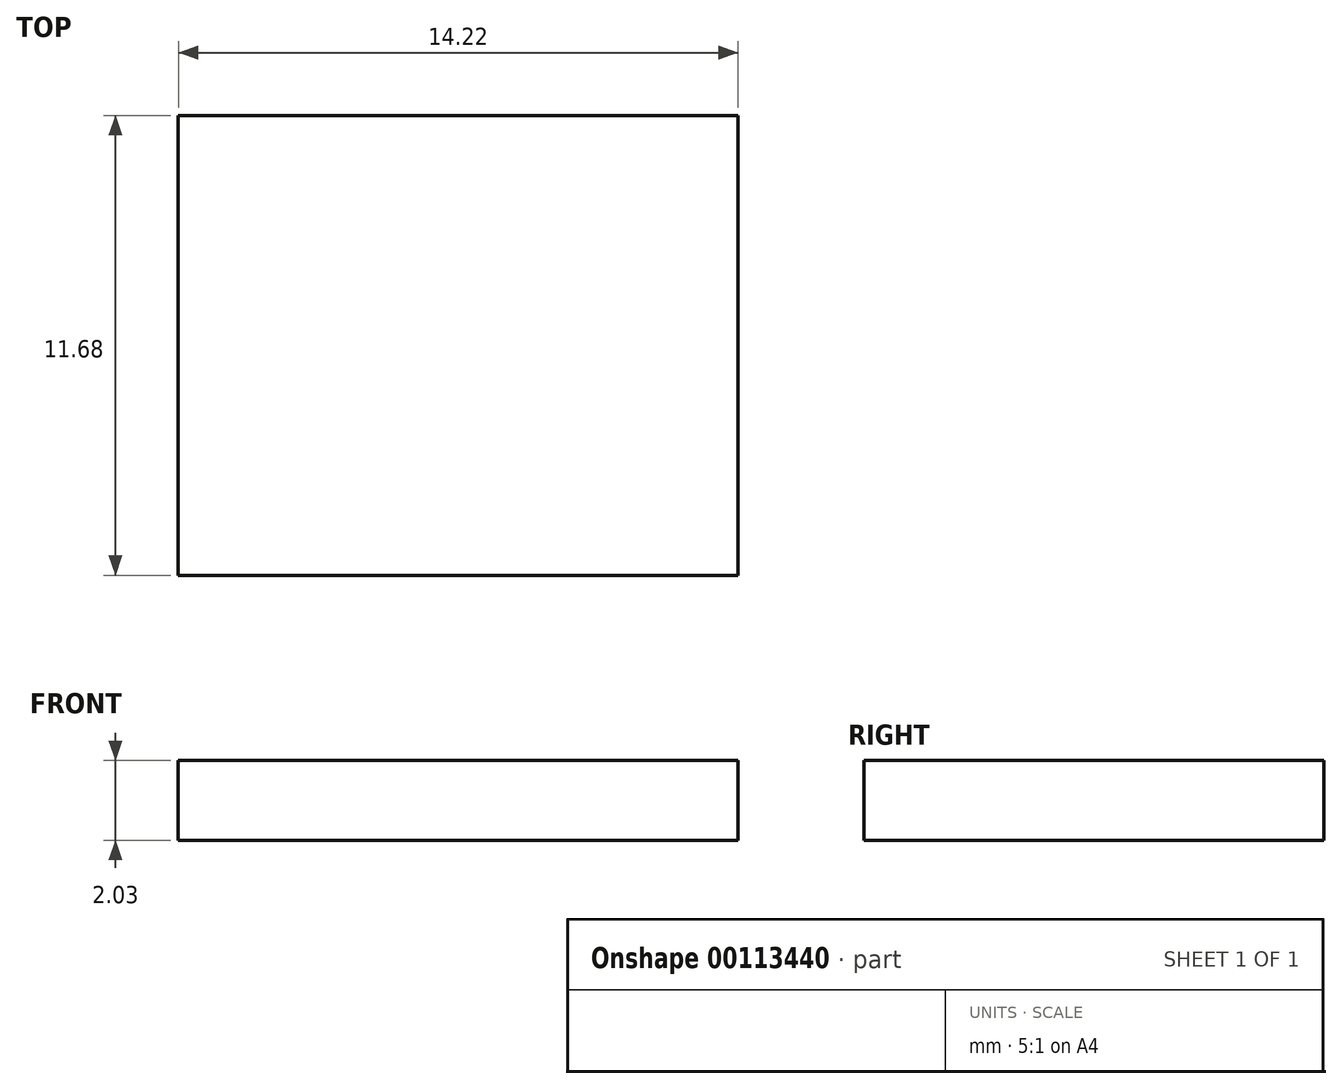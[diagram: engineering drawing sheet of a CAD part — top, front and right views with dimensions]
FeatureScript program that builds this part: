
annotation { "Feature Type Name" : "Feature", "Feature Type Description" : "" }
export const myFeature = defineFeature(function(context is Context, id is Id, definition is map)
    precondition{}
    {
        {
            var Q0;
            Q0=qCreatedBy(makeId("Top.planeOp"),FACE);
            var sketch = newSketch(context, id + "F0", { "sketchPlane" : qUnion([Q0])});
            skLineSegment(sketch, "E0.bottom", {"start": v(7.11, 5.84) * mm, "end": v(-7.11, 5.84) * mm});
            skLineSegment(sketch, "E0.top", {"start": v(7.11, -5.84) * mm, "end": v(-7.11, -5.84) * mm});
            skLineSegment(sketch, "E0.left", {"start": v(7.11, 5.84) * mm, "end": v(7.11, -5.84) * mm});
            skLineSegment(sketch, "E0.right", {"start": v(-7.11, 5.84) * mm, "end": v(-7.11, -5.84) * mm});
            skPoint(sketch, "E0.middle", {"position": v(0, 0) * mm});
            skSolve(sketch);
        }
        {
            var Q0;
            Q0=makeQuery(id+"F0.imprint","IMPRINT",FACE,{"disambiguationData":[TD([[makeQuery(id+"F0.imprint","IMPRINT",EDGE,{"derivedFrom":sQuery(id+"F0.wireOp",EDGE,"E0.bottom")}),1.0]])]});
            extrude(context, id + "F1", {"entities" : qUnion([Q0]), "depth" : 2.03 * mm});
        }
    });
